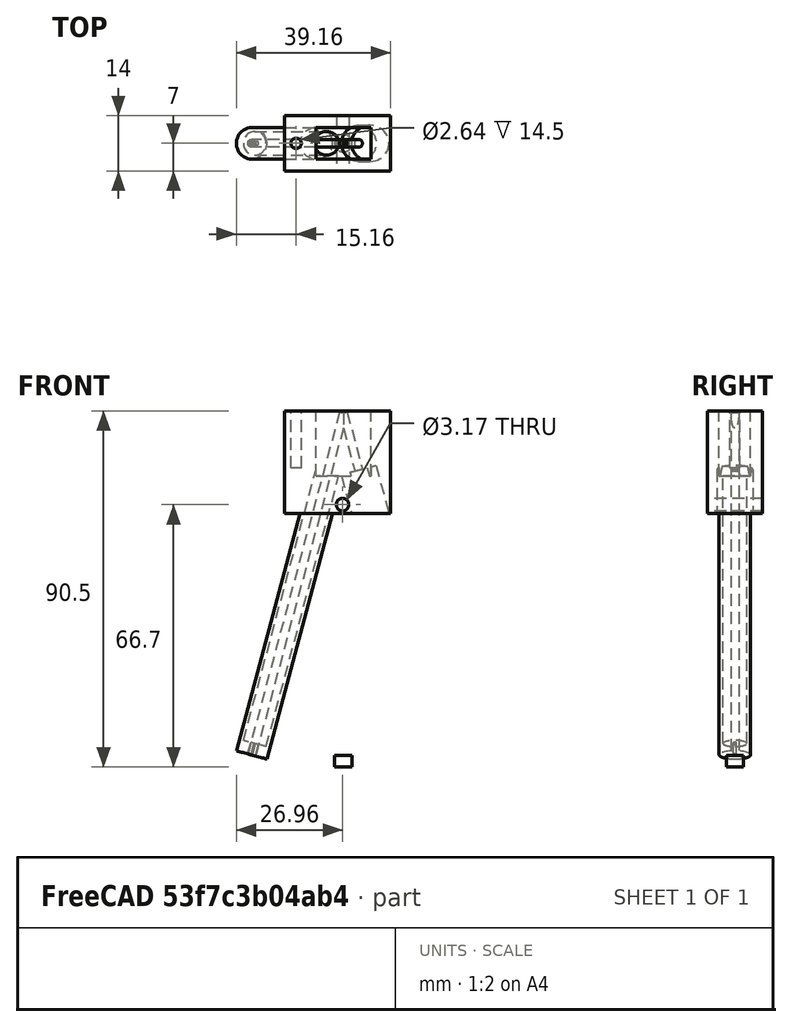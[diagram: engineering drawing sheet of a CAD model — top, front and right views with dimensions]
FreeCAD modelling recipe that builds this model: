
FCSTD DOCUMENT  (FreeCAD 0.16R)
Label: atomic_force_microscope
License: All rights reserved
LicenseURL: http://en.wikipedia.org/wiki/All_rights_reserved
objects: Part::Cylinder×10, Part::MultiFuse×3, Part::Box×2, Part::Cut×1
note: 16 computed .brp shape members not serialized (recipe doc carries the construction recipe); baked Part::Feature solids carry a one-line shape summary decoded from their .brp

FEATURE [Part::Cylinder] Cylinder  label="Laser"
  Angle = 360
  Height = 15
  Placement = pos=(3.88,0,-14.5) rot=(0,1,0;2.87979rad)
  Radius = 4.59
  expr: Placement.Rotation.Angle = 180 - 15
  expr: Radius = 8.779999999999999 / 2 + 0.2
FEATURE [Part::Cylinder] Cylinder001  label="CdS"
  Angle = 360
  Height = 3
  Placement = pos=(0,0,-90) rot=(0,0,1;0rad)
  Radius = 2.2
  expr: Radius = 4.4 / 2
FEATURE [Part::Box] Box  label="Housing"
  Height = 26
  Length = 27
  Placement = pos=(-15,-7,-25.5) rot=(0,0,1;0rad)
  Width = 14
FEATURE [Part::Cylinder] Cylinder002  label="Cylinder"
  Angle = 360
  Height = 90
  Placement = pos=(0,0,0) rot=(0,1,0;0.261799rad)
  Radius = 1
FEATURE [Part::Cylinder] Cylinder003  label="Cylinder001"
  Angle = 360
  Height = 15
  Placement = pos=(0,0,0) rot=(0,-1,0;0.261799rad)
  Radius = 1
FEATURE [Part::MultiFuse] Fusion  label="Beam"
  Placement = pos=(0,0,0) rot=(0,1,0;3.14159rad)
  Shapes = -> [Cylinder002,Cylinder003]
FEATURE [Part::Box] Box001  label="Cube"
  Height = 19
  Length = 14
  Placement = pos=(-7,-4,-16) rot=(0,0,1;0rad)
  Width = 8
FEATURE [Part::Cylinder] Cylinder004  label="Screw"
  Angle = 360
  Height = 15
  Placement = pos=(-12,0,-14) rot=(0,0,1;0rad)
  Radius = 1.32
  expr: Radius = 1.19 + 0.13
FEATURE [Part::Cylinder] Cylinder005  label="OpticalBarrel"
  Angle = 360
  Height = 70
  Placement = pos=(-23.3,0,-86.9) rot=(0,1,0;0.261799rad)
  Radius = 4
FEATURE [Part::Cylinder] Cylinder006  label="OpticalBarrelCut"
  Angle = 360
  Height = 113
  Placement = pos=(-22.5,0,-84) rot=(0,1,0;0.261799rad)
  Radius = 3
FEATURE [Part::Cylinder] Cylinder007  label="OpticalBarrel002"
  Angle = 360
  Height = 10
  Placement = pos=(-24,0,-92) rot=(0,1,0;0.261799rad)
  Radius = 0.4
FEATURE [Part::Cylinder] Cylinder008  label="OpticalBarrel003"
  Angle = 360
  Height = 10
  Placement = pos=(-25.3,0,-92) rot=(0,1,0;0.261799rad)
  Radius = 0.4
FEATURE [Part::MultiFuse] Fusion001
  Shapes = -> [Box,Cylinder005]
FEATURE [Part::Cylinder] Cylinder009  label="Mount"
  Angle = 360
  Height = 32
  Placement = pos=(-0.2,24,-23.3) rot=(1,0,0;1.5708rad)
  Radius = 1.5875
  expr: Radius = 3.175 / 2
FEATURE [Part::MultiFuse] Fusion002
  Shapes = -> [Cylinder,Cylinder004,Cylinder006,Cylinder007,Cylinder008,Box001,Cylinder009]
FEATURE [Part::Cut] Cut
  Base = -> Fusion001
  Tool = -> Fusion002
